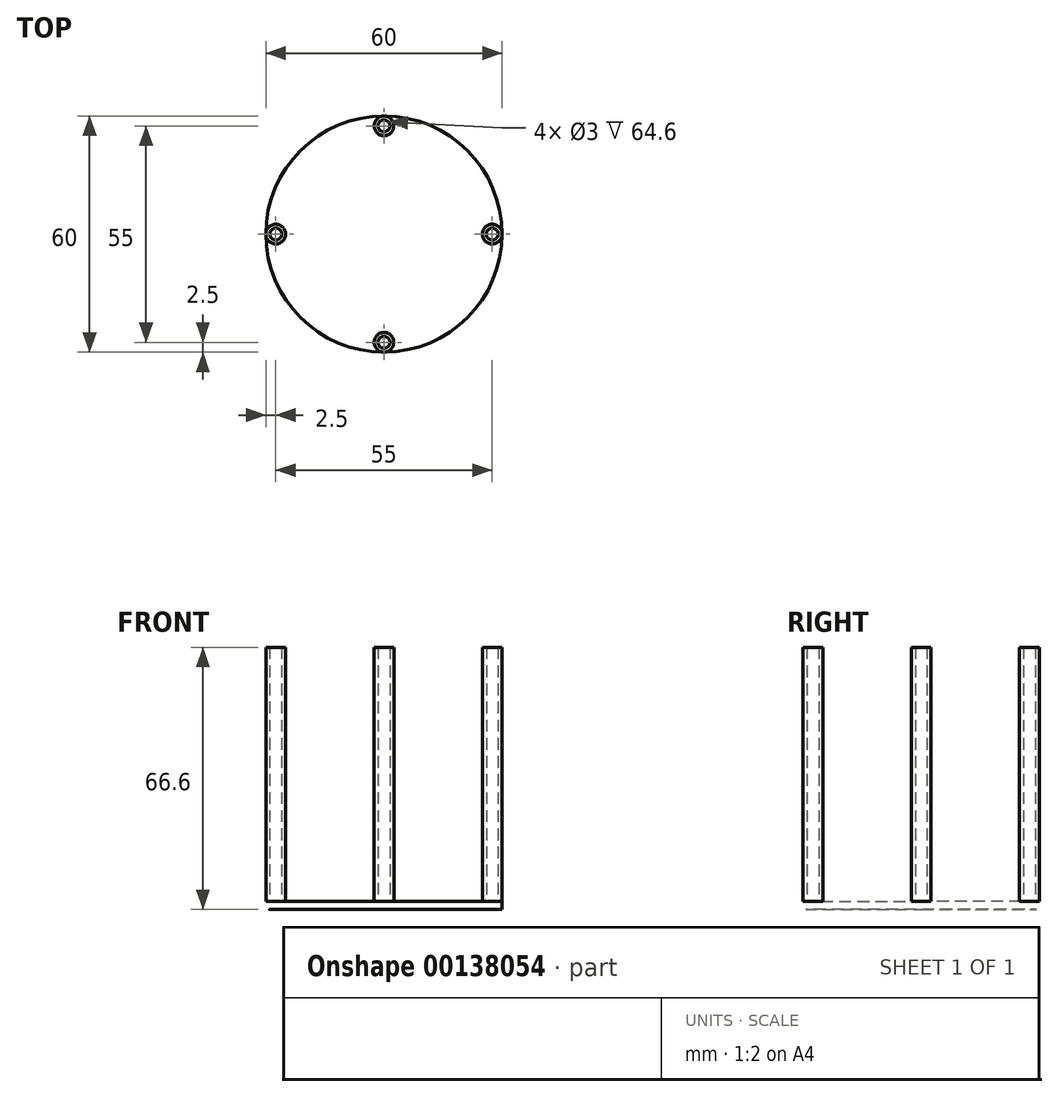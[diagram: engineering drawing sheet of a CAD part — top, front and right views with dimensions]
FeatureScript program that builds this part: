
annotation { "Feature Type Name" : "Feature", "Feature Type Description" : "" }
export const myFeature = defineFeature(function(context is Context, id is Id, definition is map)
    precondition{}
    {
        {
            var Q0;
            Q0=qCreatedBy(makeId("Top.planeOp"),FACE);
            var sketch = newSketch(context, id + "F0", { "sketchPlane" : qUnion([Q0])});
            skCircle(sketch, "E0", {"center": v(0, 0) * mm, "radius": 25 * mm});
            skCircle(sketch, "E1.0", {"center": v(0, 0) * mm, "radius": 30 * mm});
            skLineSegment(sketch, "E2", {"start": v(0, 30) * mm, "end": v(0, 25) * mm, "construction": true});
            skLineSegment(sketch, "E3", {"start": v(25, 0) * mm, "end": v(30, 0) * mm, "construction": true});
            skLineSegment(sketch, "E4", {"start": v(0, -30) * mm, "end": v(0, -25) * mm, "construction": true});
            skLineSegment(sketch, "E5", {"start": v(-25, 0) * mm, "end": v(-30, 0) * mm, "construction": true});
            skPoint(sketch, "E6", {"position": v(0, 27.5) * mm});
            skPoint(sketch, "E7", {"position": v(27.5, 0) * mm});
            skPoint(sketch, "E8", {"position": v(0, -27.5) * mm});
            skPoint(sketch, "E9", {"position": v(-27.5, 0) * mm});
            skCircle(sketch, "E10", {"center": v(0, 27.5) * mm, "radius": 2.5 * mm});
            skCircle(sketch, "E11", {"center": v(27.5, 0) * mm, "radius": 2.5 * mm});
            skCircle(sketch, "E12", {"center": v(0, -27.5) * mm, "radius": 2.5 * mm});
            skCircle(sketch, "E13", {"center": v(-27.5, 0) * mm, "radius": 2.5 * mm});
            skCircle(sketch, "E14.0", {"center": v(0, 27.5) * mm, "radius": 1.5 * mm});
            skCircle(sketch, "E15.0", {"center": v(27.5, 0) * mm, "radius": 1.5 * mm});
            skCircle(sketch, "E16.0", {"center": v(0, -27.5) * mm, "radius": 1.5 * mm});
            skCircle(sketch, "E17.0", {"center": v(-27.5, 0) * mm, "radius": 1.5 * mm});
            skSolve(sketch);
        }
        {
            var Q0;
            {var subQ0=sQuery(id+"F0.wireOp",EDGE,"E0");var subQ1=makeQuery(id+"F0.imprint","INTERSECT",VERTEX,{"derivedFrom":[subQ0,sQuery(id+"F0.wireOp",EDGE,"E10")]});Q0=makeQuery(id+"F0.imprint","IMPRINT",FACE,{"disambiguationData":[TD([[makeQuery(id+"F0.imprint","IMPRINT",EDGE,{"disambiguationData":[TD([[subQ1,1.0]])],"derivedFrom":subQ0}),1.0]])]});}
            var Q1;
            {var subQ0=sQuery(id+"F0.wireOp",EDGE,"E10");var subQ1=sQuery(id+"F0.wireOp",EDGE,"E0");var subQ2=makeQuery(id+"F0.imprint","INTERSECT",VERTEX,{"derivedFrom":[subQ1,subQ0]});Q1=makeQuery(id+"F0.imprint","IMPRINT",FACE,{"disambiguationData":[TD([[makeQuery(id+"F0.imprint","IMPRINT",EDGE,{"disambiguationData":[TD([[subQ2,-1.0]])],"derivedFrom":subQ1}),-1.0]])]});}
            var Q2;
            {var subQ0=sQuery(id+"F0.wireOp",EDGE,"E10");var subQ1=sQuery(id+"F0.wireOp",EDGE,"E0");var subQ2=makeQuery(id+"F0.imprint","INTERSECT",VERTEX,{"derivedFrom":[subQ1,subQ0]});Q2=makeQuery(id+"F0.imprint","IMPRINT",FACE,{"disambiguationData":[TD([[makeQuery(id+"F0.imprint","IMPRINT",EDGE,{"disambiguationData":[TD([[subQ2,1.0]])],"derivedFrom":subQ1}),-1.0]])]});}
            var Q3;
            {var subQ0=sQuery(id+"F0.wireOp",EDGE,"E11");var subQ1=sQuery(id+"F0.wireOp",EDGE,"E0");var subQ2=makeQuery(id+"F0.imprint","INTERSECT",VERTEX,{"derivedFrom":[subQ1,subQ0]});Q3=makeQuery(id+"F0.imprint","IMPRINT",FACE,{"disambiguationData":[TD([[makeQuery(id+"F0.imprint","IMPRINT",EDGE,{"disambiguationData":[TD([[subQ2,1.0]])],"derivedFrom":subQ1}),-1.0]])]});}
            var Q4;
            {var subQ0=sQuery(id+"F0.wireOp",EDGE,"E13");var subQ1=sQuery(id+"F0.wireOp",EDGE,"E0");var subQ2=makeQuery(id+"F0.imprint","INTERSECT",VERTEX,{"derivedFrom":[subQ1,subQ0]});Q4=makeQuery(id+"F0.imprint","IMPRINT",FACE,{"disambiguationData":[TD([[makeQuery(id+"F0.imprint","IMPRINT",EDGE,{"disambiguationData":[TD([[subQ2,-1.0]])],"derivedFrom":subQ1}),-1.0]])]});}
            var Q5;
            Q5=makeQuery(id+"F0.imprint","IMPRINT",FACE,{"disambiguationData":[TD([[makeQuery(id+"F0.imprint","IMPRINT",EDGE,{"derivedFrom":sQuery(id+"F0.wireOp",EDGE,"E14.0")}),-1.0]])]});
            var Q6;
            Q6=makeQuery(id+"F0.imprint","IMPRINT",FACE,{"disambiguationData":[TD([[makeQuery(id+"F0.imprint","IMPRINT",EDGE,{"derivedFrom":sQuery(id+"F0.wireOp",EDGE,"E14.0")}),1.0]])]});
            var Q7;
            Q7=makeQuery(id+"F0.imprint","IMPRINT",FACE,{"disambiguationData":[TD([[makeQuery(id+"F0.imprint","IMPRINT",EDGE,{"derivedFrom":sQuery(id+"F0.wireOp",EDGE,"E15.0")}),-1.0]])]});
            var Q8;
            Q8=makeQuery(id+"F0.imprint","IMPRINT",FACE,{"disambiguationData":[TD([[makeQuery(id+"F0.imprint","IMPRINT",EDGE,{"derivedFrom":sQuery(id+"F0.wireOp",EDGE,"E15.0")}),1.0]])]});
            var Q9;
            Q9=makeQuery(id+"F0.imprint","IMPRINT",FACE,{"disambiguationData":[TD([[makeQuery(id+"F0.imprint","IMPRINT",EDGE,{"derivedFrom":sQuery(id+"F0.wireOp",EDGE,"E16.0")}),-1.0]])]});
            var Q10;
            Q10=makeQuery(id+"F0.imprint","IMPRINT",FACE,{"disambiguationData":[TD([[makeQuery(id+"F0.imprint","IMPRINT",EDGE,{"derivedFrom":sQuery(id+"F0.wireOp",EDGE,"E16.0")}),1.0]])]});
            var Q11;
            Q11=makeQuery(id+"F0.imprint","IMPRINT",FACE,{"disambiguationData":[TD([[makeQuery(id+"F0.imprint","IMPRINT",EDGE,{"derivedFrom":sQuery(id+"F0.wireOp",EDGE,"E17.0")}),1.0]])]});
            var Q12;
            Q12=makeQuery(id+"F0.imprint","IMPRINT",FACE,{"disambiguationData":[TD([[makeQuery(id+"F0.imprint","IMPRINT",EDGE,{"derivedFrom":sQuery(id+"F0.wireOp",EDGE,"E17.0")}),-1.0]])]});
            extrude(context, id + "F1", {"entities" : qUnion([Q0, Q1, Q2, Q3, Q4, Q5, Q6, Q7, Q8, Q9, Q10, Q11, Q12]), "depth" : 2 * mm});
        }
        {
            var Q0;
            Q0=makeQuery(id+"F0.imprint","IMPRINT",FACE,{"disambiguationData":[TD([[makeQuery(id+"F0.imprint","IMPRINT",EDGE,{"derivedFrom":sQuery(id+"F0.wireOp",EDGE,"E16.0")}),-1.0]])]});
            var Q1;
            Q1=makeQuery(id+"F0.imprint","IMPRINT",FACE,{"disambiguationData":[TD([[makeQuery(id+"F0.imprint","IMPRINT",EDGE,{"derivedFrom":sQuery(id+"F0.wireOp",EDGE,"E17.0")}),-1.0]])]});
            var Q2;
            Q2=makeQuery(id+"F0.imprint","IMPRINT",FACE,{"disambiguationData":[TD([[makeQuery(id+"F0.imprint","IMPRINT",EDGE,{"derivedFrom":sQuery(id+"F0.wireOp",EDGE,"E14.0")}),-1.0]])]});
            var Q3;
            Q3=makeQuery(id+"F0.imprint","IMPRINT",FACE,{"disambiguationData":[TD([[makeQuery(id+"F0.imprint","IMPRINT",EDGE,{"derivedFrom":sQuery(id+"F0.wireOp",EDGE,"E15.0")}),-1.0]])]});
            extrude(context, id + "F2", {"entities" : qUnion([Q0, Q1, Q2, Q3]), "operationType" : NewBodyOperationType.ADD, "depth" : 66.6 * mm});
        }
    });
